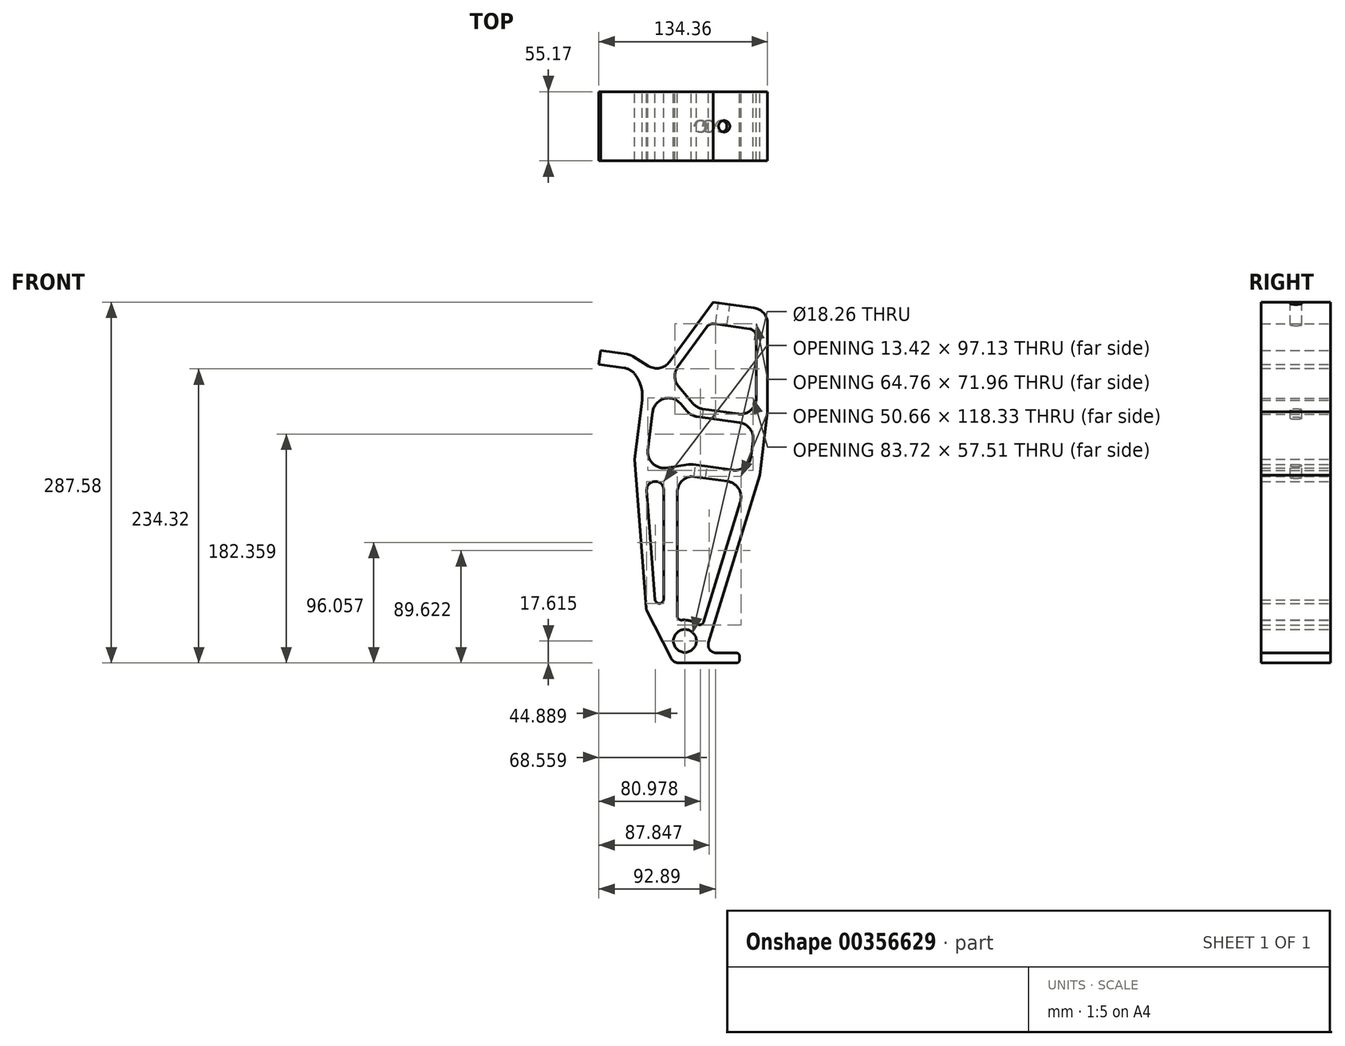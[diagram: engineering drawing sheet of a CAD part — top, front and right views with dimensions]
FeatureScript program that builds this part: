
annotation { "Feature Type Name" : "Feature", "Feature Type Description" : "" }
export const myFeature = defineFeature(function(context is Context, id is Id, definition is map)
    precondition{}
    {
        {
            var Q0;
            Q0=qCreatedBy(makeId("Front.planeOp"),FACE);
            var sketch = newSketch(context, id + "F0", { "sketchPlane" : qUnion([Q0])});
            skLineSegment(sketch, "E0", {"start": v(12.5, 56.7) * mm, "end": v(57.92, 56.7) * mm});
            skLineSegment(sketch, "E1", {"start": v(60.46, 59.25) * mm, "end": v(60.46, 62.25) * mm});
            skLineSegment(sketch, "E2", {"start": v(57.92, 64.79) * mm, "end": v(41.86, 64.79) * mm});
            skLineSegment(sketch, "E3", {"start": v(35.79, 73) * mm, "end": v(76.57, 206.4) * mm});
            skLineSegment(sketch, "E4", {"start": v(76.57, 206.4) * mm, "end": v(82.76, 256.82) * mm});
            skLineSegment(sketch, "E5", {"start": v(82.76, 256.82) * mm, "end": v(82.76, 327.14) * mm});
            skLineSegment(sketch, "E6", {"start": v(5.7, 60.9) * mm, "end": v(-13.43, 98.84) * mm});
            skLineSegment(sketch, "E7", {"start": v(-13.95, 100.74) * mm, "end": v(-22.94, 219.16) * mm});
            skLineSegment(sketch, "E8", {"start": v(76.57, 206.4) * mm, "end": v(142.08, 206.4) * mm});
            skPoint(sketch, "E9.visualSharp", {"position": v(33.28, 64.79) * mm});
            skArc(sketch, "E9.filletArc", {"start": v(35.79, 73) * mm, "mid": v(36.76, 67.36) * mm, "end": v(41.86, 64.79) * mm});
            skPoint(sketch, "E10.visualSharp", {"position": v(60.46, 64.79) * mm});
            skArc(sketch, "E10.filletArc", {"start": v(60.46, 62.25) * mm, "mid": v(59.71, 64.04) * mm, "end": v(57.92, 64.79) * mm});
            skPoint(sketch, "E11.visualSharp", {"position": v(60.46, 56.7) * mm});
            skArc(sketch, "E11.filletArc", {"start": v(57.92, 56.7) * mm, "mid": v(59.71, 57.45) * mm, "end": v(60.46, 59.25) * mm});
            skPoint(sketch, "E12.visualSharp", {"position": v(7.8, 56.7) * mm});
            skArc(sketch, "E12.filletArc", {"start": v(5.7, 60.9) * mm, "mid": v(8.5, 57.84) * mm, "end": v(12.5, 56.7) * mm});
            skPoint(sketch, "E13.visualSharp", {"position": v(-13.88, 99.74) * mm});
            skArc(sketch, "E13.filletArc", {"start": v(-13.95, 100.74) * mm, "mid": v(-13.78, 99.77) * mm, "end": v(-13.43, 98.84) * mm});
            skCircle(sketch, "E14", {"center": v(16.96, 74.32) * mm, "radius": 9.13 * mm});
            skLineSegment(sketch, "E15", {"start": v(23.47, 214.88) * mm, "end": v(55.24, 210.41) * mm});
            skLineSegment(sketch, "E16", {"start": v(19.85, 214.87) * mm, "end": v(1.99, 212.24) * mm});
            skLineSegment(sketch, "E17.0", {"start": v(-6.8, 107.17) * mm, "end": v(-13.42, 194.4) * mm});
            skLineSegment(sketch, "E18.trimOffspring", {"start": v(-7.27, 201.28) * mm, "end": v(-8.01, 201.17) * mm});
            skLineSegment(sketch, "E19", {"start": v(0, 195) * mm, "end": v(0, 107.61) * mm});
            skArc(sketch, "E20.filletArc", {"start": v(0, 195) * mm, "mid": v(-2.2, 199.8) * mm, "end": v(-7.27, 201.28) * mm});
            skArc(sketch, "E21.filletArc", {"start": v(-8.01, 201.17) * mm, "mid": v(-12.05, 198.85) * mm, "end": v(-13.42, 194.4) * mm});
            skLineSegment(sketch, "E22", {"start": v(-22.94, 219.16) * mm, "end": v(-17.18, 266.09) * mm});
            skPoint(sketch, "E23.visualSharp", {"position": v(-4.85, 302.13) * mm});
            skLineSegment(sketch, "E24", {"start": v(26.47, 253.04) * mm, "end": v(60.34, 248.28) * mm});
            skLineSegment(sketch, "E25", {"start": v(18.52, 257.43) * mm, "end": v(13.58, 263.3) * mm});
            skLineSegment(sketch, "E26.0", {"start": v(31.33, 259.1) * mm, "end": v(59.4, 255.15) * mm});
            skLineSegment(sketch, "E27.0", {"start": v(-12.46, 226.36) * mm, "end": v(-8.74, 256.67) * mm});
            skArc(sketch, "E28.filletArc", {"start": v(13.58, 263.3) * mm, "mid": v(0.25, 267.3) * mm, "end": v(-8.74, 256.67) * mm});
            skArc(sketch, "E29.filletArc", {"start": v(-12.46, 226.36) * mm, "mid": v(-8.73, 215.72) * mm, "end": v(1.99, 212.24) * mm});
            skLineSegment(sketch, "E30.0", {"start": v(69.62, 221.44) * mm, "end": v(71.18, 234.15) * mm});
            skPoint(sketch, "E31.visualSharp", {"position": v(72.7, 246.54) * mm});
            skArc(sketch, "E31.filletArc", {"start": v(71.18, 234.15) * mm, "mid": v(68.65, 243.43) * mm, "end": v(60.34, 248.28) * mm});
            skArc(sketch, "E32.filletArc", {"start": v(55.24, 210.41) * mm, "mid": v(64.74, 212.92) * mm, "end": v(69.62, 221.44) * mm});
            skLineSegment(sketch, "E33", {"start": v(39.32, 344.29) * mm, "end": v(71.83, 339.72) * mm});
            skPoint(sketch, "E34.visualSharp", {"position": v(73.77, 253.13) * mm});
            skArc(sketch, "E34.filletArc", {"start": v(59.4, 255.15) * mm, "mid": v(68.81, 257.62) * mm, "end": v(73.67, 266.04) * mm});
            skPoint(sketch, "E35.visualSharp", {"position": v(82.76, 338.18) * mm});
            skArc(sketch, "E35.filletArc", {"start": v(82.76, 327.14) * mm, "mid": v(79.65, 335.47) * mm, "end": v(71.83, 339.72) * mm});
            skLineSegment(sketch, "E36", {"start": v(4.8, 296.78) * mm, "end": v(39.32, 344.29) * mm});
            skArc(sketch, "E37", {"start": v(-6.8, 107.17) * mm, "mid": v(-3.2, 104.2) * mm, "end": v(0, 107.61) * mm});
            skLineSegment(sketch, "E38", {"start": v(-96.98, 305.95) * mm, "end": v(-51.6, 305.95) * mm, "construction": true});
            skLineSegment(sketch, "E39", {"start": v(-51.6, 333.21) * mm, "end": v(-51.6, 294.71) * mm, "construction": true});
            skLineSegment(sketch, "E40", {"start": v(-50.05, 305.73) * mm, "end": v(-29.32, 302.82) * mm});
            skLineSegment(sketch, "E41.0", {"start": v(-51.6, 294.71) * mm, "end": v(-31.35, 291.87) * mm});
            skLineSegment(sketch, "E42", {"start": v(-51.6, 294.71) * mm, "end": v(-51.6, 286.86) * mm, "construction": true});
            skLineSegment(sketch, "E43", {"start": v(-51.6, 294.71) * mm, "end": v(-50.05, 305.73) * mm});
            skPoint(sketch, "E44.orphan", {"position": v(-51.6, 305.95) * mm});
            skArc(sketch, "E45", {"start": v(-17.18, 266.09) * mm, "mid": v(-18.06, 277.3) * mm, "end": v(-23.24, 287.27) * mm});
            skLineSegment(sketch, "E46", {"start": v(-12.16, 293.45) * mm, "end": v(-24.4, 301.03) * mm});
            skPoint(sketch, "E47.visualSharp", {"position": v(-2.13, 287.24) * mm});
            skArc(sketch, "E47.filletArc", {"start": v(-12.16, 293.45) * mm, "mid": v(-3.02, 291.79) * mm, "end": v(4.8, 296.78) * mm});
            skPoint(sketch, "E48.visualSharp", {"position": v(-26.67, 302.44) * mm});
            skArc(sketch, "E48.filletArc", {"start": v(-24.4, 301.03) * mm, "mid": v(-26.76, 302.18) * mm, "end": v(-29.32, 302.82) * mm});
            skPoint(sketch, "E49.visualSharp", {"position": v(-27.2, 291.28) * mm});
            skArc(sketch, "E49.filletArc", {"start": v(-23.24, 287.27) * mm, "mid": v(-26.86, 290.34) * mm, "end": v(-31.35, 291.87) * mm});
            skLineSegment(sketch, "E50", {"start": v(16.96, 74.32) * mm, "end": v(49.92, 342.8) * mm, "construction": true});
            skLineSegment(sketch, "E51.0", {"start": v(11.33, 292.8) * mm, "end": v(34.28, 324.4) * mm});
            skLineSegment(sketch, "E52.0", {"start": v(73.67, 266.04) * mm, "end": v(73.67, 316.74) * mm});
            skLineSegment(sketch, "E53", {"start": v(40.3, 326.95) * mm, "end": v(68.2, 323.03) * mm});
            skPoint(sketch, "E54.visualSharp", {"position": v(73.67, 322.26) * mm});
            skArc(sketch, "E54.filletArc", {"start": v(73.67, 316.74) * mm, "mid": v(72.11, 320.9) * mm, "end": v(68.2, 323.03) * mm});
            skPoint(sketch, "E55.visualSharp", {"position": v(36.53, 327.48) * mm});
            skArc(sketch, "E55.filletArc", {"start": v(40.3, 326.95) * mm, "mid": v(36.94, 326.5) * mm, "end": v(34.28, 324.4) * mm});
            skLineSegment(sketch, "E56", {"start": v(23.38, 263.5) * mm, "end": v(11.89, 277.15) * mm});
            skPoint(sketch, "E57.visualSharp", {"position": v(26.51, 259.78) * mm});
            skArc(sketch, "E57.filletArc", {"start": v(23.38, 263.5) * mm, "mid": v(26.95, 260.56) * mm, "end": v(31.33, 259.1) * mm});
            skPoint(sketch, "E58.visualSharp", {"position": v(5.48, 284.75) * mm});
            skArc(sketch, "E58.filletArc", {"start": v(11.33, 292.8) * mm, "mid": v(8.9, 284.87) * mm, "end": v(11.89, 277.15) * mm});
            skPoint(sketch, "E59.visualSharp", {"position": v(21.66, 253.71) * mm});
            skArc(sketch, "E59.filletArc", {"start": v(18.52, 257.43) * mm, "mid": v(22.1, 254.5) * mm, "end": v(26.47, 253.04) * mm});
            skArc(sketch, "E60.filletArc", {"start": v(23.47, 214.88) * mm, "mid": v(21.66, 215) * mm, "end": v(19.85, 214.87) * mm});
            skLineSegment(sketch, "E61.0", {"start": v(22.15, 205.5) * mm, "end": v(50.68, 201.49) * mm});
            skLineSegment(sketch, "E62", {"start": v(31.77, 89.4) * mm, "end": v(61.06, 185.2) * mm});
            skLineSegment(sketch, "E63", {"start": v(22.15, 205.5) * mm, "end": v(21.77, 205.44) * mm});
            skPoint(sketch, "E63.endSnap0", {"position": v(10.92, 213.56) * mm});
            skLineSegment(sketch, "E64", {"start": v(10.92, 192.88) * mm, "end": v(10.92, 94.12) * mm});
            skArc(sketch, "E65", {"start": v(26.96, 87.69) * mm, "mid": v(20.94, 90.4) * mm, "end": v(14.36, 90.95) * mm});
            skPoint(sketch, "E66.visualSharp", {"position": v(10.92, 203.85) * mm});
            skArc(sketch, "E66.filletArc", {"start": v(21.77, 205.44) * mm, "mid": v(14, 201.18) * mm, "end": v(10.92, 192.88) * mm});
            skPoint(sketch, "E67.visualSharp", {"position": v(65.4, 199.42) * mm});
            skArc(sketch, "E67.filletArc", {"start": v(61.06, 185.2) * mm, "mid": v(59.63, 195.74) * mm, "end": v(50.68, 201.49) * mm});
            skPoint(sketch, "E68.visualSharp", {"position": v(10.92, 90.35) * mm});
            skArc(sketch, "E68.filletArc", {"start": v(10.92, 94.12) * mm, "mid": v(11.95, 91.78) * mm, "end": v(14.36, 90.95) * mm});
            skPoint(sketch, "E69.visualSharp", {"position": v(30.36, 84.79) * mm});
            skArc(sketch, "E69.filletArc", {"start": v(26.96, 87.69) * mm, "mid": v(29.8, 87.33) * mm, "end": v(31.77, 89.4) * mm});
            skSolve(sketch);
        }
        {
            var Q0;
            Q0=makeQuery(id+"F0.imprint","IMPRINT",FACE,{"disambiguationData":[TD([[makeQuery(id+"F0.imprint","IMPRINT",EDGE,{"derivedFrom":sQuery(id+"F0.wireOp",EDGE,"E0")}),1.0]])]});
            extrude(context, id + "F1", {"entities" : qUnion([Q0]), "depth" : 55.17 * mm});
        }
        {
            var Q0;
            Q0=makeQuery(id+"F1.opExtrude","SWEPT_FACE",FACE,{"disambiguationData":[OSD([sQuery(id+"F0.wireOp",EDGE,"E33")])]});
            var sketch = newSketch(context, id + "F2", { "sketchPlane" : qUnion([Q0])});
            skCircle(sketch, "E70", {"center": v(0, -27.58) * mm, "radius": 4.6 * mm});
            skLineSegment(sketch, "E71", {"start": v(23.85, -27.58) * mm, "end": v(-8.98, -27.58) * mm, "construction": true});
            skLineSegment(sketch, "E72", {"start": v(7.44, 0) * mm, "end": v(7.44, -55.17) * mm, "construction": true});
            skLineSegment(sketch, "E73", {"start": v(7.44, -55.17) * mm, "end": v(0, -55.17) * mm, "construction": true});
            skLineSegment(sketch, "E74", {"start": v(0, -55.17) * mm, "end": v(0, 0) * mm, "construction": true});
            skSolve(sketch);
        }
        {
            var Q0;
            Q0=makeQuery(id+"F2.imprint","IMPRINT",FACE,{"disambiguationData":[TD([[makeQuery(id+"F2.imprint","IMPRINT",EDGE,{"derivedFrom":sQuery(id+"F2.wireOp",EDGE,"E70")}),1.0]])]});
            extrude(context, id + "F3", {"entities" : qUnion([Q0]), "operationType" : NewBodyOperationType.REMOVE, "oppositeDirection" : true, "depth" : 152.4 * mm});
        }
    });
